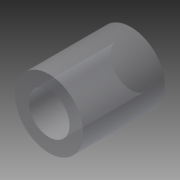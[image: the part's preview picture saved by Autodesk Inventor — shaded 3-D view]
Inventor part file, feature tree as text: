
AUTODESK INVENTOR PART (.ipt)
format: ipt  version: 2014 SP1 (Build 180222100, 222)  size: 80,896 bytes
history: native  units: in
note: dims shown in document units (in); Inventor stores cm internally (conversion verified against a paired STEP export)
features: extrude x1, sketch x1
ambient origin geometry x8: Origin, YZ Plane, XZ Plane, XY Plane, X Axis, Y Axis, Z Axis, Center Point
bodies: Solid1 (feature_tree)
feature tree (2):
  extrude  "Extrusion1"  Depth=0.75in
  sketch  "Sketch1"  dims[d0=0.375in d1=0.625in d2=0.75in d3=0.0in]
